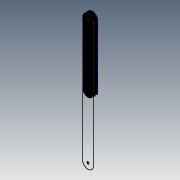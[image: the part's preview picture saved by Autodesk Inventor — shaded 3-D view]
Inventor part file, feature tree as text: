
AUTODESK INVENTOR PART (.ipt)
format: ipt  version: 2015 (Build 190159000, 159)  size: 93,184 bytes
history: native  units: mm
features: other x5, sketch x2, reference x2, extrude x1
ambient origin geometry x8: Origin, YZ Plane, XZ Plane, XY Plane, X Axis, Y Axis, Z Axis, Center Point
bodies: Solid1 (feature_tree)
feature tree (10):
  other  "Blocks"
  extrude  "Extrusion1"  Depth=50.0mm
  sketch  "Sketch2"  dims[d2=10.0mm d3=10.0mm d4=20.0mm d5=0.0mm d6=285.0mm]
  other  "DXF"
  sketch  "Sketch1"  dims[d0=50.0mm d1=50.0mm]
  reference  "Reference1"
  reference  "Reference2"
  other  "Block1"
  other  "Block1:1"
  other  "Block1:2"
